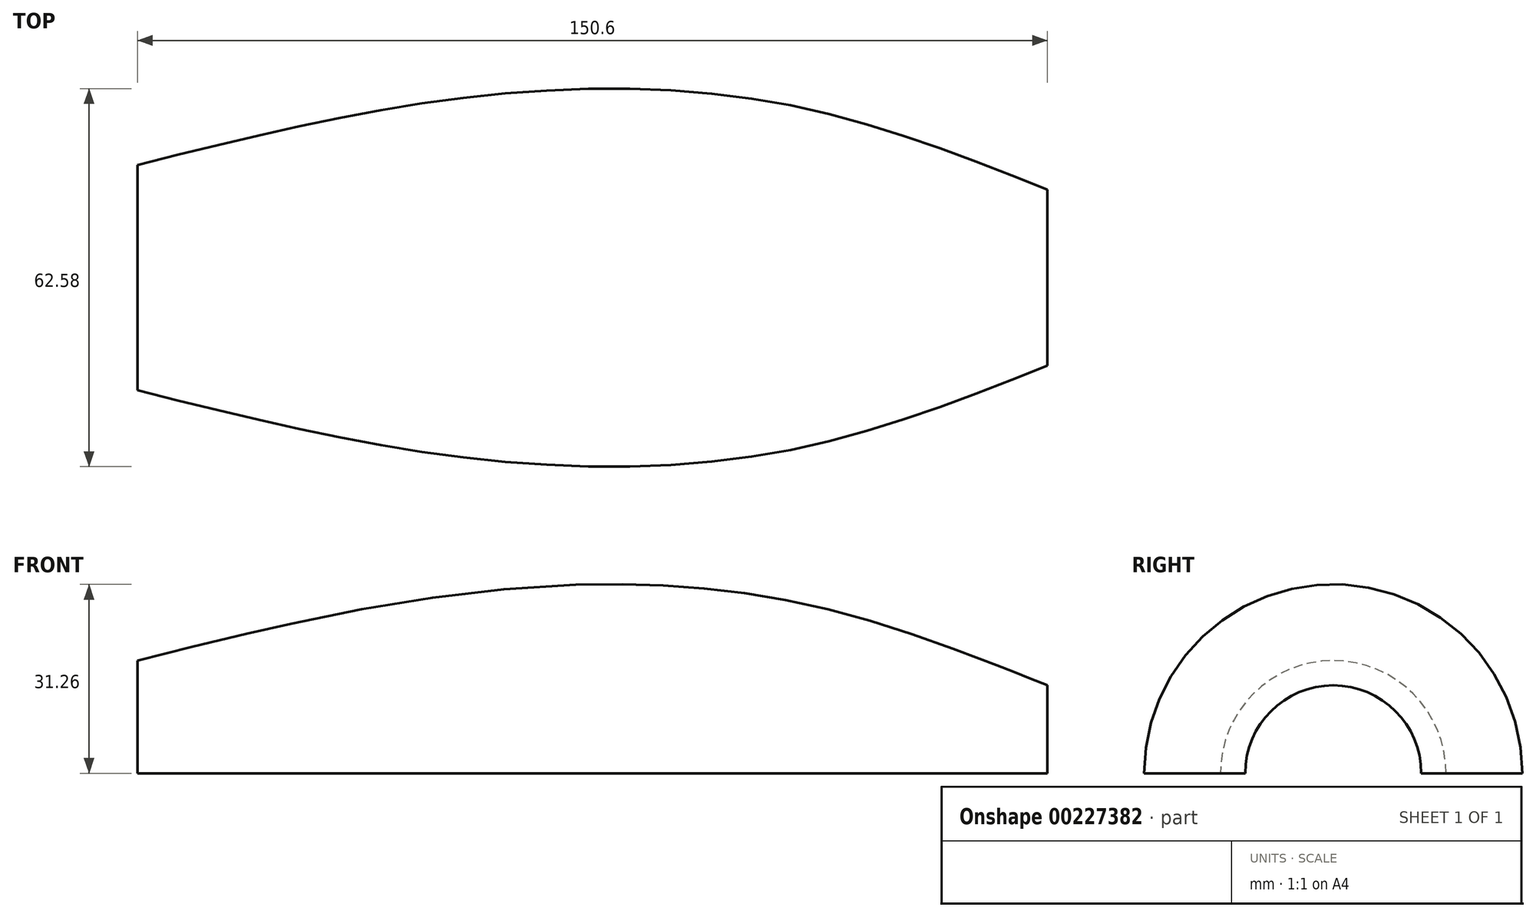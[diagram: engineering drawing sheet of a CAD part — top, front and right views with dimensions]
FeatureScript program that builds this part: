
annotation { "Feature Type Name" : "Feature", "Feature Type Description" : "" }
export const myFeature = defineFeature(function(context is Context, id is Id, definition is map)
    precondition{}
    {
        {
            var Q0;
            Q0=qCreatedBy(makeId("Top.planeOp"),FACE);
            var sketch = newSketch(context, id + "F0", { "sketchPlane" : qUnion([Q0])});
            skLineSegment(sketch, "E0", {"start": v(-75.02, 0) * mm, "end": v(44.98, 0) * mm});
            skSolve(sketch);
        }
        {
            var Q0;
            Q0=qCreatedBy(makeId("Top.planeOp"),FACE);
            var sketch = newSketch(context, id + "F1", { "sketchPlane" : qUnion([Q0])});
            skFitSpline(sketch, "E1", {"points": [v(-75.58, 18.66) * mm, v(-22.4, 29.67) * mm, v(30.42, 28.92) * mm, v(75.02, 14.56) * mm], "startDerivative": vector(153.62, 38.35) * mm, "endDerivative": vector(135.72, -54) * mm});
            skSolve(sketch);
        }
        {
            var Q0;
            Q0=sQuery(id+"F1.wireOp",EDGE,"E1");
            var Q1;
            Q1=sQuery(id+"F0.wireOp",EDGE,"E0");
            revolve(context, id + "F2", {"bodyType" : ToolBodyType.SURFACE, "surfaceEntities" : qUnion([Q0]), "axis" : qUnion([Q1]), "revolveType" : RevolveType.ONE_DIRECTION, "angle" : 180 * degree});
        }
    });
